# Revit family: xFaucet-Single_Control-American_Standard-Delancey_4279.300
name_source: partatom
category: Plumbing Fixtures
revit_build: Autodesk Revit 2014 (Build: 20130308_1515(x64)
units: mm (PartAtom-declared; Revit-internal decimal feet)

## types (1)
- 4279.300
    ADA Compliant = Yes
    Assembly Code = D2020300
    CW Connection = Yes
    CWFU = 1.5
    Cold Water Connection Diameter = 3/8"
    Default Elevation = 0"
    Description = Delancey Single Control Kitchen Faucet With Pull-Down Spray
    Escutcheon Plate = No
    Finish = Metal-American Standard-075-Stainless Steel
    Flow Rate = 1.5 gpm (5.7L/min)
    HW Connection = Yes
    HWFU = 1.5
    Height = 16 11/16"
    Hot Water Connection Diameter = 3/8"
    Installation Type = Deck Mounted
    Length = 10 3/4"
    Manufacturer = American Standard
    Material = Metal-American Standard-075-Stainless Steel
    Model = 4279.300
    Price = Prices may vary. Please consult Manufacturer Representative for most up-to-date price list.
    Product Documentation Link = https://www.americanstandard-us.com
    Product Page URL = https://www.americanstandard-us.com
    URL = http://www.americanstandard-us.com
    Vent Connection = No
    WFU = 0
    Waste Connection = No
    Width = 8 11/16"

## geometry (parser evidence)
native form markers: Sweep x1
no freeform markers — native parametric forms only
